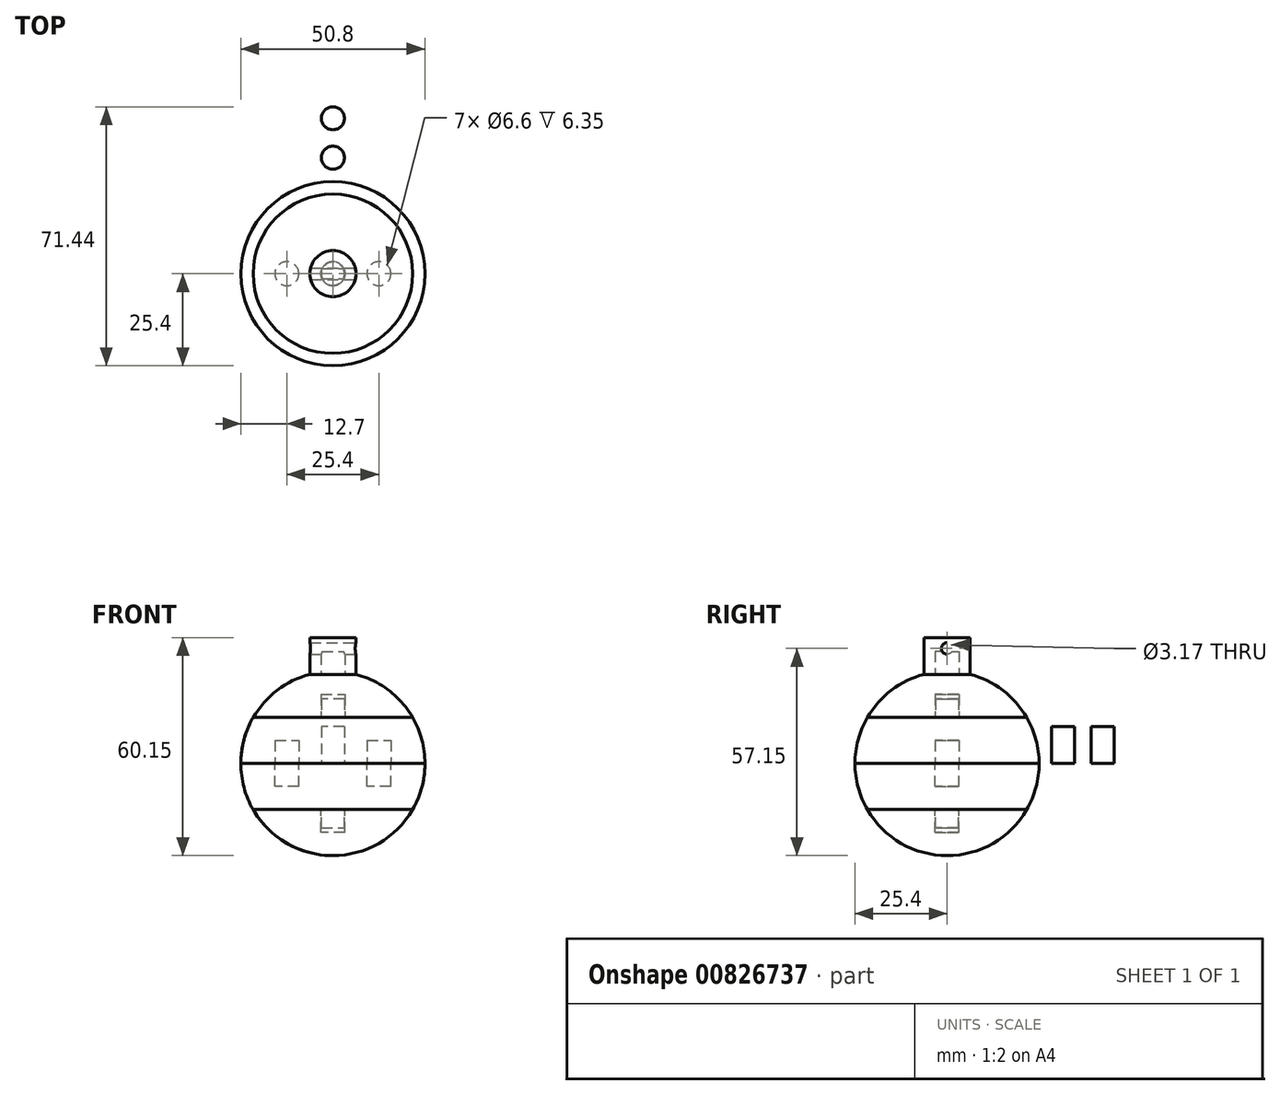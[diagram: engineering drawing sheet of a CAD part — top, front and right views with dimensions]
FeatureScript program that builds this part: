
annotation { "Feature Type Name" : "Feature", "Feature Type Description" : "" }
export const myFeature = defineFeature(function(context is Context, id is Id, definition is map)
    precondition{}
    {
        {
            var Q0;
            Q0=qCreatedBy(makeId("Front.planeOp"),FACE);
            var sketch = newSketch(context, id + "F0", { "sketchPlane" : qUnion([Q0])});
            skArc(sketch, "E0", {"start": v(0, -25.4) * mm, "mid": v(12.7, -22) * mm, "end": v(22, -12.7) * mm});
            skLineSegment(sketch, "E1", {"start": v(0, -25.4) * mm, "end": v(0, -12.7) * mm});
            skLineSegment(sketch, "E2", {"start": v(0, -12.7) * mm, "end": v(22, -12.7) * mm});
            skSolve(sketch);
        }
        {
            var Q0;
            Q0=qSketchRegion(id+"F0",true);
            var Q1;
            Q1=sQuery(id+"F0.wireOp",EDGE,"E1");
            revolve(context, id + "F1", {"entities" : qUnion([Q0]), "axis" : qUnion([Q1]), "revolveType" : RevolveType.FULL});
        }
        {
            var Q0;
            Q0=qCreatedBy(makeId("Front.planeOp"),FACE);
            var sketch = newSketch(context, id + "F2", { "sketchPlane" : qUnion([Q0])});
            skArc(sketch, "E3", {"start": v(22, -12.7) * mm, "mid": v(24.53, -6.57) * mm, "end": v(25.4, 0) * mm});
            skLineSegment(sketch, "E4", {"start": v(0, 0) * mm, "end": v(25.4, 0) * mm});
            skLineSegment(sketch, "E5", {"start": v(0, 0) * mm, "end": v(0, -12.7) * mm});
            skLineSegment(sketch, "E6", {"start": v(0, -12.7) * mm, "end": v(22, -12.7) * mm});
            skSolve(sketch);
        }
        {
            var Q0;
            Q0=qSketchRegion(id+"F2",true);
            var Q1;
            Q1=sQuery(id+"F2.wireOp",EDGE,"E5");
            revolve(context, id + "F3", {"entities" : qUnion([Q0]), "axis" : qUnion([Q1]), "revolveType" : RevolveType.FULL});
        }
        {
            var Q0;
            Q0=qCreatedBy(makeId("Front.planeOp"),FACE);
            var sketch = newSketch(context, id + "F4", { "sketchPlane" : qUnion([Q0])});
            skArc(sketch, "E7", {"start": v(25.4, 0) * mm, "mid": v(24.53, 6.57) * mm, "end": v(22, 12.7) * mm});
            skLineSegment(sketch, "E8", {"start": v(0, 0) * mm, "end": v(25.4, 0) * mm});
            skLineSegment(sketch, "E9", {"start": v(0, 0) * mm, "end": v(0, 12.7) * mm});
            skLineSegment(sketch, "E10", {"start": v(0, 12.7) * mm, "end": v(22, 12.7) * mm});
            skSolve(sketch);
        }
        {
            var Q0;
            Q0=makeQuery(id+"F4.imprint","IMPRINT",FACE,{"disambiguationData":[TD([[makeQuery(id+"F4.imprint","IMPRINT",EDGE,{"derivedFrom":sQuery(id+"F4.wireOp",EDGE,"E7")}),1.0]])]});
            var Q1;
            Q1=sQuery(id+"F4.wireOp",EDGE,"E9");
            revolve(context, id + "F5", {"entities" : qUnion([Q0]), "axis" : qUnion([Q1]), "revolveType" : RevolveType.FULL});
        }
        {
            var Q0;
            Q0=qCreatedBy(makeId("Front.planeOp"),FACE);
            var sketch = newSketch(context, id + "F6", { "sketchPlane" : qUnion([Q0])});
            skArc(sketch, "E11", {"start": v(22, 12.7) * mm, "mid": v(15.37, 20.22) * mm, "end": v(6.35, 24.6) * mm});
            skLineSegment(sketch, "E12", {"start": v(0, 24.6) * mm, "end": v(0, 12.7) * mm});
            skLineSegment(sketch, "E13", {"start": v(0, 12.7) * mm, "end": v(22, 12.7) * mm});
            skLineSegment(sketch, "E14", {"start": v(0, 24.6) * mm, "end": v(6.35, 24.6) * mm});
            skPoint(sketch, "E15.orphan", {"position": v(0, 25.4) * mm});
            skSolve(sketch);
        }
        {
            var Q0;
            Q0=qSketchRegion(id+"F6",true);
            var Q1;
            Q1=sQuery(id+"F6.wireOp",EDGE,"E12");
            revolve(context, id + "F7", {"entities" : qUnion([Q0]), "axis" : qUnion([Q1]), "revolveType" : RevolveType.FULL});
        }
        {
            var Q0;
            Q0=makeQuery(id+"F7.opRevolve","SWEPT_FACE",FACE,{"disambiguationData":[OSD([sQuery(id+"F6.wireOp",EDGE,"E14")])]});
            var sketch = newSketch(context, id + "F8", { "sketchPlane" : qUnion([Q0])});
            skCircle(sketch, "E16", {"center": v(0, 0) * mm, "radius": 3.18 * mm});
            skSolve(sketch);
        }
        {
            var Q0;
            Q0=makeQuery(id+"F8.imprint","IMPRINT",FACE,{"disambiguationData":[TD([[makeQuery(id+"F8.imprint","IMPRINT",EDGE,{"derivedFrom":sQuery(id+"F8.wireOp",EDGE,"E16")}),1.0]])]});
            extrude(context, id + "F9", {"entities" : qUnion([Q0]), "operationType" : NewBodyOperationType.ADD, "depth" : 5.08 * mm});
        }
        {
            var Q0;
            Q0=makeQuery(id+"F7.opRevolve","SWEPT_FACE",FACE,{"disambiguationData":[OSD([sQuery(id+"F6.wireOp",EDGE,"E14")])]});
            var sketch = newSketch(context, id + "F10", { "sketchPlane" : qUnion([Q0])});
            skCircle(sketch, "E17", {"center": v(0, 0) * mm, "radius": 6.35 * mm});
            skSolve(sketch);
        }
        {
            var Q0;
            Q0=qSketchRegion(id+"F10",true);
            extrude(context, id + "F11", {"entities" : qUnion([Q0]), "depth" : 10.16 * mm});
        }
        {
            var Q0;
            Q0=qCreatedBy(makeId("Right.planeOp"),FACE);
            var sketch = newSketch(context, id + "F12", { "sketchPlane" : qUnion([Q0])});
            skCircle(sketch, "E18", {"center": v(0, 31.75) * mm, "radius": 1.59 * mm});
            skSolve(sketch);
        }
        {
            var Q0;
            Q0=qSketchRegion(id+"F12",true);
            extrude(context, id + "F13", {"entities" : qUnion([Q0]), "operationType" : NewBodyOperationType.REMOVE, "oppositeDirection" : true, "depth" : 25.4 * mm, "hasSecondDirection" : true, "secondDirectionOppositeDirection" : false, "secondDirectionDepth" : 25.4 * mm});
        }
        {
            var Q0;
            Q0=makeQuery(id+"F11.opExtrude","CAP_FACE",FACE,{"disambiguationData":[OSD([sQuery(id+"F10.wireOp",EDGE,"E17")])],"isStart":true});
            var sketch = newSketch(context, id + "F14", { "sketchPlane" : qUnion([Q0])});
            skCircle(sketch, "E19", {"center": v(0, 0) * mm, "radius": 3.3 * mm});
            skSolve(sketch);
        }
        {
            var Q0;
            Q0=makeQuery(id+"F14.imprint","IMPRINT",FACE,{"disambiguationData":[TD([[makeQuery(id+"F14.imprint","IMPRINT",EDGE,{"derivedFrom":sQuery(id+"F14.wireOp",EDGE,"E19")}),1.0]])]});
            extrude(context, id + "F15", {"entities" : qUnion([Q0]), "operationType" : NewBodyOperationType.REMOVE, "oppositeDirection" : true, "depth" : 6.35 * mm});
        }
        {
            var Q0;
            Q0=makeQuery(id+"F7.opRevolve","SWEPT_FACE",FACE,{"disambiguationData":[OSD([sQuery(id+"F6.wireOp",EDGE,"E13")])]});
            var sketch = newSketch(context, id + "F16", { "sketchPlane" : qUnion([Q0])});
            skCircle(sketch, "E20", {"center": v(0, 0) * mm, "radius": 3.3 * mm});
            skSolve(sketch);
        }
        {
            var Q0;
            Q0=makeQuery(id+"F16.imprint","IMPRINT",FACE,{"disambiguationData":[TD([[makeQuery(id+"F16.imprint","IMPRINT",EDGE,{"derivedFrom":sQuery(id+"F16.wireOp",EDGE,"E20")}),1.0]])]});
            extrude(context, id + "F17", {"entities" : qUnion([Q0]), "operationType" : NewBodyOperationType.REMOVE, "oppositeDirection" : true, "depth" : 6.35 * mm});
        }
        {
            var Q0;
            Q0=makeQuery(id+"F1.opRevolve","SWEPT_FACE",FACE,{"disambiguationData":[OSD([sQuery(id+"F0.wireOp",EDGE,"E2")])]});
            var sketch = newSketch(context, id + "F18", { "sketchPlane" : qUnion([Q0])});
            skCircle(sketch, "E21", {"center": v(0, 0) * mm, "radius": 3.3 * mm});
            skSolve(sketch);
        }
        {
            var Q0;
            Q0=qSketchRegion(id+"F18",true);
            extrude(context, id + "F19", {"entities" : qUnion([Q0]), "operationType" : NewBodyOperationType.REMOVE, "oppositeDirection" : true, "depth" : 6.35 * mm});
        }
        {
            var Q0;
            Q0=makeQuery(id+"F5.opRevolve","SWEPT_FACE",FACE,{"disambiguationData":[OSD([sQuery(id+"F4.wireOp",EDGE,"E10")])]});
            var sketch = newSketch(context, id + "F20", { "sketchPlane" : qUnion([Q0])});
            skCircle(sketch, "E22", {"center": v(0, 0) * mm, "radius": 3.18 * mm});
            skSolve(sketch);
        }
        {
            var Q0;
            Q0=qSketchRegion(id+"F20",true);
            extrude(context, id + "F21", {"entities" : qUnion([Q0]), "operationType" : NewBodyOperationType.ADD, "depth" : 5.08 * mm});
        }
        {
            var Q0;
            Q0=makeQuery(id+"F3.opRevolve","SWEPT_FACE",FACE,{"disambiguationData":[OSD([sQuery(id+"F2.wireOp",EDGE,"E6")])]});
            var sketch = newSketch(context, id + "F22", { "sketchPlane" : qUnion([Q0])});
            skCircle(sketch, "E23", {"center": v(0, 0) * mm, "radius": 3.18 * mm});
            skSolve(sketch);
        }
        {
            var Q0;
            Q0=qSketchRegion(id+"F22",true);
            extrude(context, id + "F23", {"entities" : qUnion([Q0]), "operationType" : NewBodyOperationType.ADD, "depth" : 5.08 * mm});
        }
        {
            var Q0;
            Q0=makeQuery(id+"F3.opRevolve","SWEPT_FACE",FACE,{"disambiguationData":[OSD([sQuery(id+"F2.wireOp",EDGE,"E4")])]});
            var sketch = newSketch(context, id + "F24", { "sketchPlane" : qUnion([Q0])});
            skCircle(sketch, "E24", {"center": v(12.7, 0) * mm, "radius": 3.3 * mm});
            skCircle(sketch, "E25", {"center": v(-12.7, 0) * mm, "radius": 3.3 * mm});
            skSolve(sketch);
        }
        {
            var Q0;
            Q0=qSketchRegion(id+"F24",true);
            extrude(context, id + "F25", {"entities" : qUnion([Q0]), "operationType" : NewBodyOperationType.REMOVE, "oppositeDirection" : true, "depth" : 6.35 * mm});
        }
        {
            var Q0;
            Q0=qCreatedBy(makeId("Top.planeOp"),FACE);
            var sketch = newSketch(context, id + "F26", { "sketchPlane" : qUnion([Q0])});
            skCircle(sketch, "E26", {"center": v(0, 31.98) * mm, "radius": 3.18 * mm});
            skCircle(sketch, "E27", {"center": v(0, 42.87) * mm, "radius": 3.18 * mm});
            skSolve(sketch);
        }
        {
            var Q0;
            Q0=qSketchRegion(id+"F26",true);
            extrude(context, id + "F27", {"entities" : qUnion([Q0]), "depth" : 10.16 * mm});
        }
        {
            var Q0;
            Q0=makeQuery(id+"F5.opRevolve","SWEPT_FACE",FACE,{"disambiguationData":[OSD([sQuery(id+"F4.wireOp",EDGE,"E8")])]});
            var sketch = newSketch(context, id + "F28", { "sketchPlane" : qUnion([Q0])});
            skCircle(sketch, "E28", {"center": v(-12.7, 0) * mm, "radius": 3.3 * mm});
            skCircle(sketch, "E29", {"center": v(12.7, 0) * mm, "radius": 3.3 * mm});
            skPoint(sketch, "E30", {"position": v(0, 0) * mm});
            skSolve(sketch);
        }
        {
            var Q0;
            Q0=qSketchRegion(id+"F28",true);
            extrude(context, id + "F29", {"entities" : qUnion([Q0]), "operationType" : NewBodyOperationType.REMOVE, "oppositeDirection" : true, "depth" : 6.35 * mm});
        }
    });
